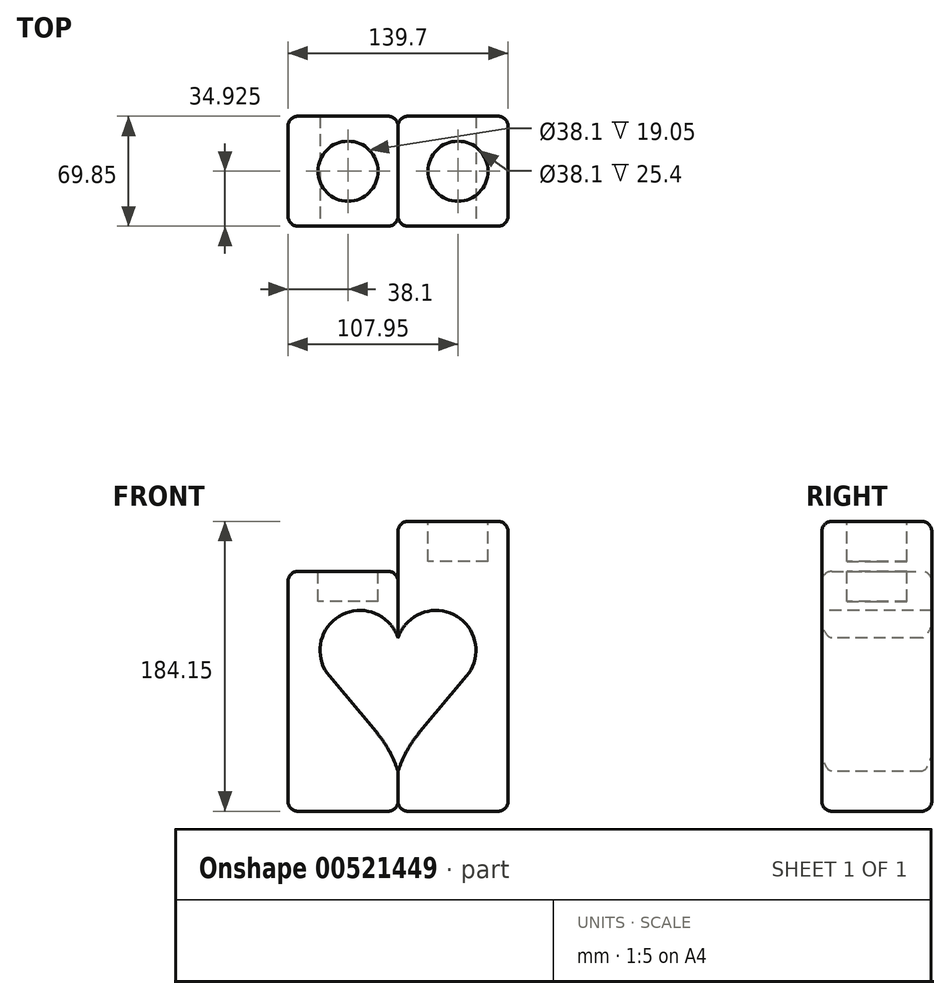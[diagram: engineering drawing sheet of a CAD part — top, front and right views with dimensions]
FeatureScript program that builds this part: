
annotation { "Feature Type Name" : "Feature", "Feature Type Description" : "" }
export const myFeature = defineFeature(function(context is Context, id is Id, definition is map)
    precondition{}
    {
        {
            var Q0;
            Q0=qCreatedBy(makeId("Top.planeOp"),FACE);
            var sketch = newSketch(context, id + "F0", { "sketchPlane" : qUnion([Q0])});
            skLineSegment(sketch, "E0.bottom", {"start": v(0, 0) * mm, "end": v(69.85, 0) * mm});
            skLineSegment(sketch, "E0.top", {"start": v(0, 69.85) * mm, "end": v(69.85, 69.85) * mm});
            skLineSegment(sketch, "E0.left", {"start": v(0, 0) * mm, "end": v(0, 69.85) * mm});
            skLineSegment(sketch, "E0.right", {"start": v(69.85, 0) * mm, "end": v(69.85, 69.85) * mm});
            skSolve(sketch);
        }
        {
            var Q0;
            Q0 = qSketchRegion(id + "F0", true);
            extrude(context, id + "F1", {"entities" : qUnion([Q0]), "depth" : 184.15 * mm, "offsetDistance" : 25.4 * mm});
        }
        {
            var Q0;
            Q0=makeQuery(id+"F1.opExtrude","SWEPT_EDGE",EDGE,{"disambiguationData":[OSD([sQuery(id+"F0.wireOp",EDGE,"E0.top"),sQuery(id+"F0.wireOp",EDGE,"E0.left")])]});
            var Q1;
            Q1=makeQuery(id+"F1.opExtrude","SWEPT_EDGE",EDGE,{"disambiguationData":[OSD([sQuery(id+"F0.wireOp",EDGE,"E0.bottom"),sQuery(id+"F0.wireOp",EDGE,"E0.left")])]});
            var Q2;
            Q2=makeQuery(id+"F1.opExtrude","SWEPT_EDGE",EDGE,{"disambiguationData":[OSD([sQuery(id+"F0.wireOp",EDGE,"E0.bottom"),sQuery(id+"F0.wireOp",EDGE,"E0.right")])]});
            var Q3;
            Q3=makeQuery(id+"F1.opExtrude","SWEPT_EDGE",EDGE,{"disambiguationData":[OSD([sQuery(id+"F0.wireOp",EDGE,"E0.top"),sQuery(id+"F0.wireOp",EDGE,"E0.right")])]});
            fillet(context, id + "F2", {"entities" : qUnion([Q0, Q1, Q2, Q3]), "radius" : 6.35 * mm, "tangentPropagation" : true, "allowEdgeOverflow" : false});
        }
        {
            var Q0;
            Q0=makeQuery(id+"F1.opExtrude","CAP_EDGE",EDGE,{"disambiguationData":[OSD([sQuery(id+"F0.wireOp",EDGE,"E0.right")])],"isStart":false});
            var Q1;
            Q1=makeQuery(id+"F1.opExtrude","SWEPT_FACE",FACE,{"disambiguationData":[OSD([sQuery(id+"F0.wireOp",EDGE,"E0.right")])]});
            fillet(context, id + "F3", {"entities" : qUnion([Q0, Q1]), "radius" : 6.35 * mm, "tangentPropagation" : true, "allowEdgeOverflow" : false});
        }
        {
            var Q0;
            Q0=qCreatedBy(makeId("Top.planeOp"),FACE);
            var sketch = newSketch(context, id + "F4", { "sketchPlane" : qUnion([Q0])});
            skLineSegment(sketch, "E1.bottom", {"start": v(0, 0) * mm, "end": v(-69.85, 0) * mm});
            skLineSegment(sketch, "E1.top", {"start": v(0, 69.85) * mm, "end": v(-69.85, 69.85) * mm});
            skLineSegment(sketch, "E1.left", {"start": v(0, 0) * mm, "end": v(0, 69.85) * mm});
            skLineSegment(sketch, "E1.right", {"start": v(-69.85, 0) * mm, "end": v(-69.85, 69.85) * mm});
            skSolve(sketch);
        }
        {
            var Q0;
            Q0 = qSketchRegion(id + "F4", true);
            extrude(context, id + "F5", {"entities" : qUnion([Q0]), "depth" : 152.4 * mm, "offsetDistance" : 25.4 * mm});
        }
        {
            var Q0;
            Q0=makeQuery(id+"F5.opExtrude","SWEPT_EDGE",EDGE,{"disambiguationData":[OSD([sQuery(id+"F4.wireOp",EDGE,"E1.bottom"),sQuery(id+"F4.wireOp",EDGE,"E1.left")])]});
            var Q1;
            Q1=makeQuery(id+"F5.opExtrude","SWEPT_EDGE",EDGE,{"disambiguationData":[OSD([sQuery(id+"F4.wireOp",EDGE,"E1.bottom"),sQuery(id+"F4.wireOp",EDGE,"E1.right")])]});
            var Q2;
            Q2=makeQuery(id+"F5.opExtrude","SWEPT_EDGE",EDGE,{"disambiguationData":[OSD([sQuery(id+"F4.wireOp",EDGE,"E1.top"),sQuery(id+"F4.wireOp",EDGE,"E1.right")])]});
            var Q3;
            Q3=makeQuery(id+"F5.opExtrude","SWEPT_EDGE",EDGE,{"disambiguationData":[OSD([sQuery(id+"F4.wireOp",EDGE,"E1.top"),sQuery(id+"F4.wireOp",EDGE,"E1.left")])]});
            fillet(context, id + "F6", {"entities" : qUnion([Q0, Q1, Q2, Q3]), "radius" : 6.35 * mm, "tangentPropagation" : true, "allowEdgeOverflow" : false});
        }
        {
            var Q0;
            Q0=makeQuery(id+"F5.opExtrude","CAP_EDGE",EDGE,{"disambiguationData":[OSD([sQuery(id+"F4.wireOp",EDGE,"E1.top")])],"isStart":false});
            var Q1;
            Q1=makeQuery(id+"F5.opExtrude","SWEPT_FACE",FACE,{"disambiguationData":[OSD([sQuery(id+"F4.wireOp",EDGE,"E1.right")])]});
            fillet(context, id + "F7", {"entities" : qUnion([Q0, Q1]), "radius" : 6.35 * mm, "tangentPropagation" : true, "allowEdgeOverflow" : false});
        }
        {
            var Q0;
            Q0=makeQuery(id+"F1.opExtrude","CAP_FACE",FACE,{"disambiguationData":[OSD([sQuery(id+"F0.wireOp",EDGE,"E0.bottom"),sQuery(id+"F0.wireOp",EDGE,"E0.top"),sQuery(id+"F0.wireOp",EDGE,"E0.left"),sQuery(id+"F0.wireOp",EDGE,"E0.right")])],"isStart":false});
            var sketch = newSketch(context, id + "F8", { "sketchPlane" : qUnion([Q0])});
            skCircle(sketch, "E2", {"center": v(38.1, 34.93) * mm, "radius": 19.05 * mm});
            skPoint(sketch, "E2.centerSnap0", {"position": v(6.35, 34.92) * mm});
            skSolve(sketch);
        }
        {
            var Q0;
            Q0 = qSketchRegion(id + "F8", true);
            extrude(context, id + "F9", {"entities" : qUnion([Q0]), "operationType" : NewBodyOperationType.REMOVE, "oppositeDirection" : true, "depth" : 25.4 * mm, "offsetDistance" : 25.4 * mm});
        }
        {
            var Q0;
            Q0=makeQuery(id+"F1.opExtrude","SWEPT_FACE",FACE,{"disambiguationData":[OSD([sQuery(id+"F0.wireOp",EDGE,"E0.bottom")])]});
            var sketch = newSketch(context, id + "F10", { "sketchPlane" : qUnion([Q0])});
            skArc(sketch, "E3", {"start": v(43.59, 85.82) * mm, "mid": v(36.48, 124.35) * mm, "end": v(0, 110.08) * mm});
            skLineSegment(sketch, "E4", {"start": v(24.13, 102.15) * mm, "end": v(-44.2, 102.15) * mm, "construction": true});
            skArc(sketch, "E5", {"start": v(0, 110.08) * mm, "mid": v(-36.48, 124.35) * mm, "end": v(-43.59, 85.82) * mm});
            skLineSegment(sketch, "E6", {"start": v(43.59, 85.82) * mm, "end": v(14.02, 50.59) * mm});
            skLineSegment(sketch, "E7", {"start": v(-14.02, 50.59) * mm, "end": v(-43.59, 85.82) * mm});
            skArc(sketch, "E8", {"start": v(14.02, 50.59) * mm, "mid": v(5.8, 38.66) * mm, "end": v(0, 25.4) * mm});
            skArc(sketch, "E9", {"start": v(0, 25.4) * mm, "mid": v(-5.8, 38.66) * mm, "end": v(-14.02, 50.59) * mm});
            skLineSegment(sketch, "E10", {"start": v(72.4, 1.6) * mm, "end": v(-72.39, 1.6) * mm, "construction": true});
            skPoint(sketch, "E11.orphan", {"position": v(0, 33.88) * mm});
            skLineSegment(sketch, "E12", {"start": v(-62.31, 133.35) * mm, "end": v(-9.9, 133.35) * mm, "construction": true});
            skSolve(sketch);
        }
        {
            var Q0;
            Q0 = qSketchRegion(id + "F10", true);
            extrude(context, id + "F11", {"entities" : qUnion([Q0]), "operationType" : NewBodyOperationType.REMOVE, "oppositeDirection" : true, "depth" : 76.2 * mm, "offsetDistance" : 25.4 * mm});
        }
        {
            var Q0;
            Q0=makeQuery(id+"F5.opExtrude","CAP_FACE",FACE,{"disambiguationData":[OSD([sQuery(id+"F4.wireOp",EDGE,"E1.bottom"),sQuery(id+"F4.wireOp",EDGE,"E1.top"),sQuery(id+"F4.wireOp",EDGE,"E1.left"),sQuery(id+"F4.wireOp",EDGE,"E1.right")])],"isStart":false});
            var sketch = newSketch(context, id + "F12", { "sketchPlane" : qUnion([Q0])});
            skCircle(sketch, "E13", {"center": v(-31.75, 34.93) * mm, "radius": 19.05 * mm});
            skPoint(sketch, "E13.centerSnap0", {"position": v(-63.5, 34.93) * mm});
            skSolve(sketch);
        }
        {
            var Q0;
            Q0 = qSketchRegion(id + "F12", true);
            extrude(context, id + "F13", {"entities" : qUnion([Q0]), "operationType" : NewBodyOperationType.REMOVE, "oppositeDirection" : true, "depth" : 19.05 * mm, "offsetDistance" : 25.4 * mm});
        }
    });
